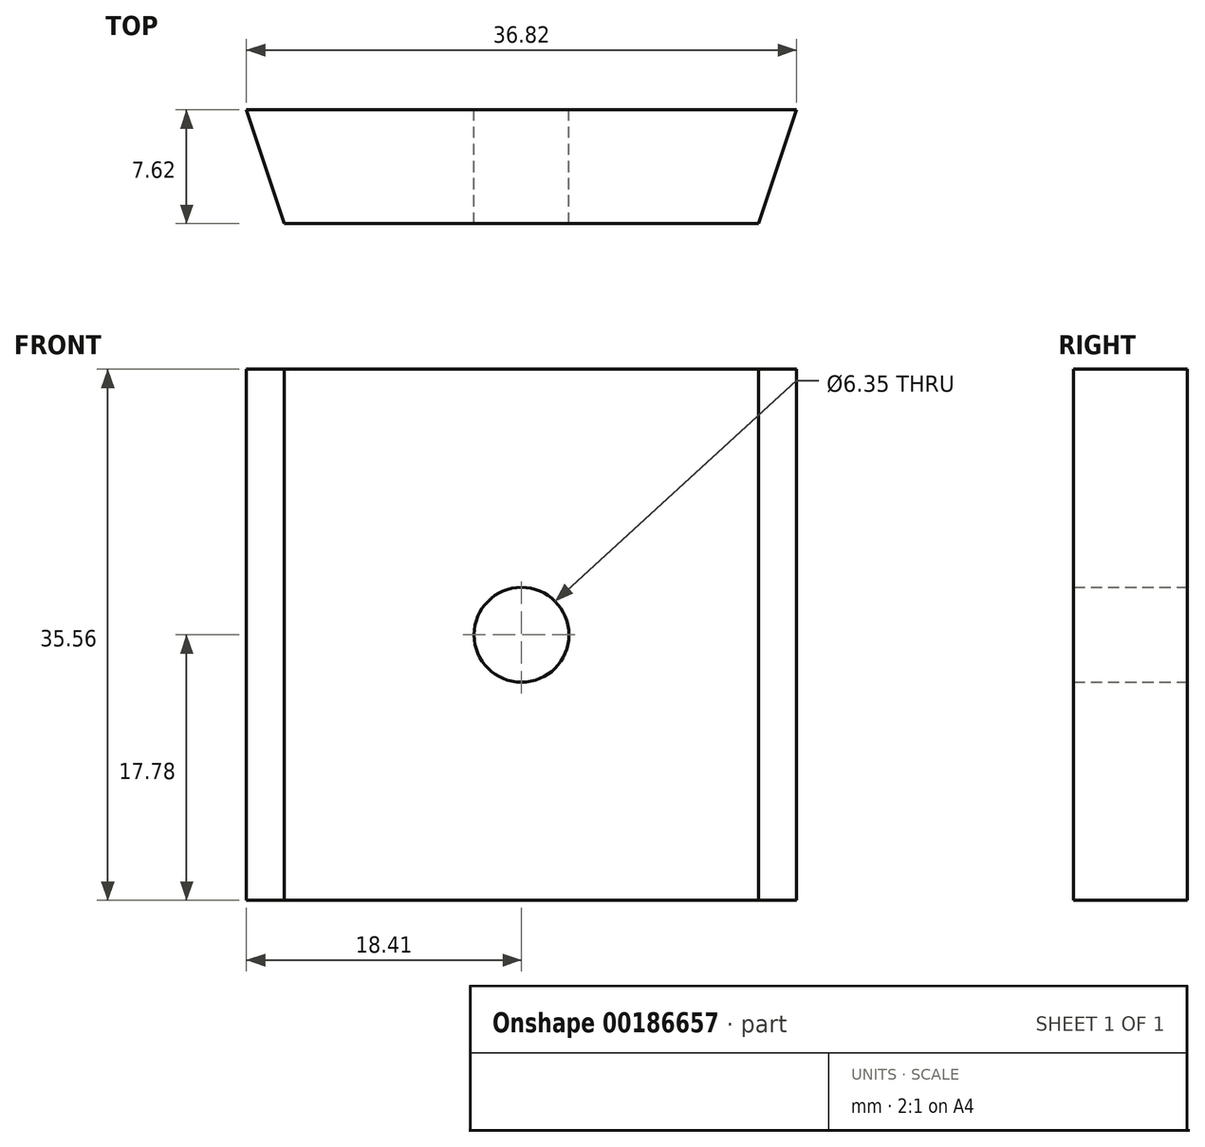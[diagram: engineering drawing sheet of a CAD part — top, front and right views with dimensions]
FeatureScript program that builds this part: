
annotation { "Feature Type Name" : "Feature", "Feature Type Description" : "" }
export const myFeature = defineFeature(function(context is Context, id is Id, definition is map)
    precondition{}
    {
        {
            var Q0;
            Q0=qCreatedBy(makeId("Front.planeOp"),FACE);
            var sketch = newSketch(context, id + "F0", { "sketchPlane" : qUnion([Q0])});
            skLineSegment(sketch, "E0.bottom", {"start": v(18.42, 17.78) * mm, "end": v(-18.41, 17.78) * mm});
            skLineSegment(sketch, "E0.top", {"start": v(18.42, -17.78) * mm, "end": v(-18.41, -17.78) * mm});
            skLineSegment(sketch, "E0.left", {"start": v(18.42, 17.78) * mm, "end": v(18.42, -17.78) * mm});
            skLineSegment(sketch, "E0.right", {"start": v(-18.41, 17.78) * mm, "end": v(-18.41, -17.78) * mm});
            skPoint(sketch, "E0.middle", {"position": v(0, 0) * mm});
            skLineSegment(sketch, "E1", {"start": v(18.42, 17.78) * mm, "end": v(15.88, 17.78) * mm, "construction": true});
            skLineSegment(sketch, "E2", {"start": v(18.42, -17.78) * mm, "end": v(15.88, -17.78) * mm, "construction": true});
            skLineSegment(sketch, "E3", {"start": v(15.88, 17.78) * mm, "end": v(15.88, -17.78) * mm, "construction": true});
            skLineSegment(sketch, "E4", {"start": v(-18.41, 17.78) * mm, "end": v(-15.88, 17.78) * mm, "construction": true});
            skLineSegment(sketch, "E5", {"start": v(-15.88, 17.78) * mm, "end": v(-15.88, -17.78) * mm, "construction": true});
            skLineSegment(sketch, "E6", {"start": v(-15.88, -17.78) * mm, "end": v(-18.41, -17.78) * mm, "construction": true});
            skCircle(sketch, "E7", {"center": v(0, 0) * mm, "radius": 3.18 * mm, "construction": true});
            skSolve(sketch);
        }
        {
            var Q0;
            Q0=qCreatedBy(makeId("Front.planeOp"),FACE);
            cPlane(context, id + "F1", {"entities" : qUnion([Q0]), "cplaneType" : CPlaneType.OFFSET, "offset" : 7.62 * mm, "width" : 152.4 * mm, "height" : 152.4 * mm});
        }
        {
            var Q0;
            Q0=qCreatedBy(id+"F1.planeOp",FACE);
            var sketch = newSketch(context, id + "F2", { "sketchPlane" : qUnion([Q0])});
            skLineSegment(sketch, "E8.bottom", {"start": v(-15.88, 17.78) * mm, "end": v(15.88, 17.78) * mm});
            skLineSegment(sketch, "E8.top", {"start": v(-15.87, -17.78) * mm, "end": v(15.88, -17.78) * mm});
            skLineSegment(sketch, "E8.left", {"start": v(-15.87, 17.78) * mm, "end": v(-15.87, -17.78) * mm});
            skLineSegment(sketch, "E8.right", {"start": v(15.88, 17.78) * mm, "end": v(15.88, -17.78) * mm});
            skCircle(sketch, "E9", {"center": v(0, 0) * mm, "radius": 3.18 * mm, "construction": true});
            skSolve(sketch);
        }
        {
            var Q0;
            Q0=makeQuery(id+"F2.imprint","IMPRINT",FACE,{"disambiguationData":[TD([[makeQuery(id+"F2.imprint","IMPRINT",EDGE,{"derivedFrom":sQuery(id+"F2.wireOp",EDGE,"E8.bottom")}),-1.0]])]});
            var Q1;
            Q1=makeQuery(id+"F0.imprint","IMPRINT",FACE,{"disambiguationData":[TD([[makeQuery(id+"F0.imprint","IMPRINT",EDGE,{"derivedFrom":sQuery(id+"F0.wireOp",EDGE,"E0.bottom")}),1.0]])]});
            loft(context, id + "F3", {"sheetProfilesArray" : [{ "sheetProfileEntities" : qUnion([Q0]) }, { "sheetProfileEntities" : qUnion([Q1]) }]});
        }
        {
            var Q0;
            Q0=makeQuery(id+"F0.imprint","IMPRINT",FACE,{"disambiguationData":[TD([[makeQuery(id+"F0.imprint","IMPRINT",EDGE,{"derivedFrom":sQuery(id+"F0.wireOp",EDGE,"E0.bottom")}),1.0]])]});
            var sketch = newSketch(context, id + "F4", { "sketchPlane" : qUnion([Q0])});
            skCircle(sketch, "E10", {"center": v(0, 0) * mm, "radius": 3.18 * mm});
            skCircle(sketch, "E11", {"center": v(0, 0) * mm, "radius": 10.48 * mm});
            skSolve(sketch);
        }
        {
            var Q0;
            Q0=makeQuery(id+"F4.imprint","IMPRINT",FACE,{"disambiguationData":[TD([[makeQuery(id+"F4.imprint","IMPRINT",EDGE,{"derivedFrom":sQuery(id+"F4.wireOp",EDGE,"E10")}),1.0]])]});
            var Q1;
            Q1=makeQuery(id+"F3.opLoft","CAP_FACE",FACE,{"disambiguationData":[OSD([makeQuery(id+"F2.imprint","IMPRINT",FACE,{"disambiguationData":[TD([[makeQuery(id+"F2.imprint","IMPRINT",EDGE,{"derivedFrom":sQuery(id+"F2.wireOp",EDGE,"E8.bottom")}),-1.0]])]})])],"isStart":true});
            extrude(context, id + "F5", {"entities" : qUnion([Q0]), "operationType" : NewBodyOperationType.REMOVE, "endBound" : BoundingType.UP_TO_SURFACE, "endBoundEntityFace" : qUnion([Q1]), "depth" : 25.4 * mm});
        }
    });
